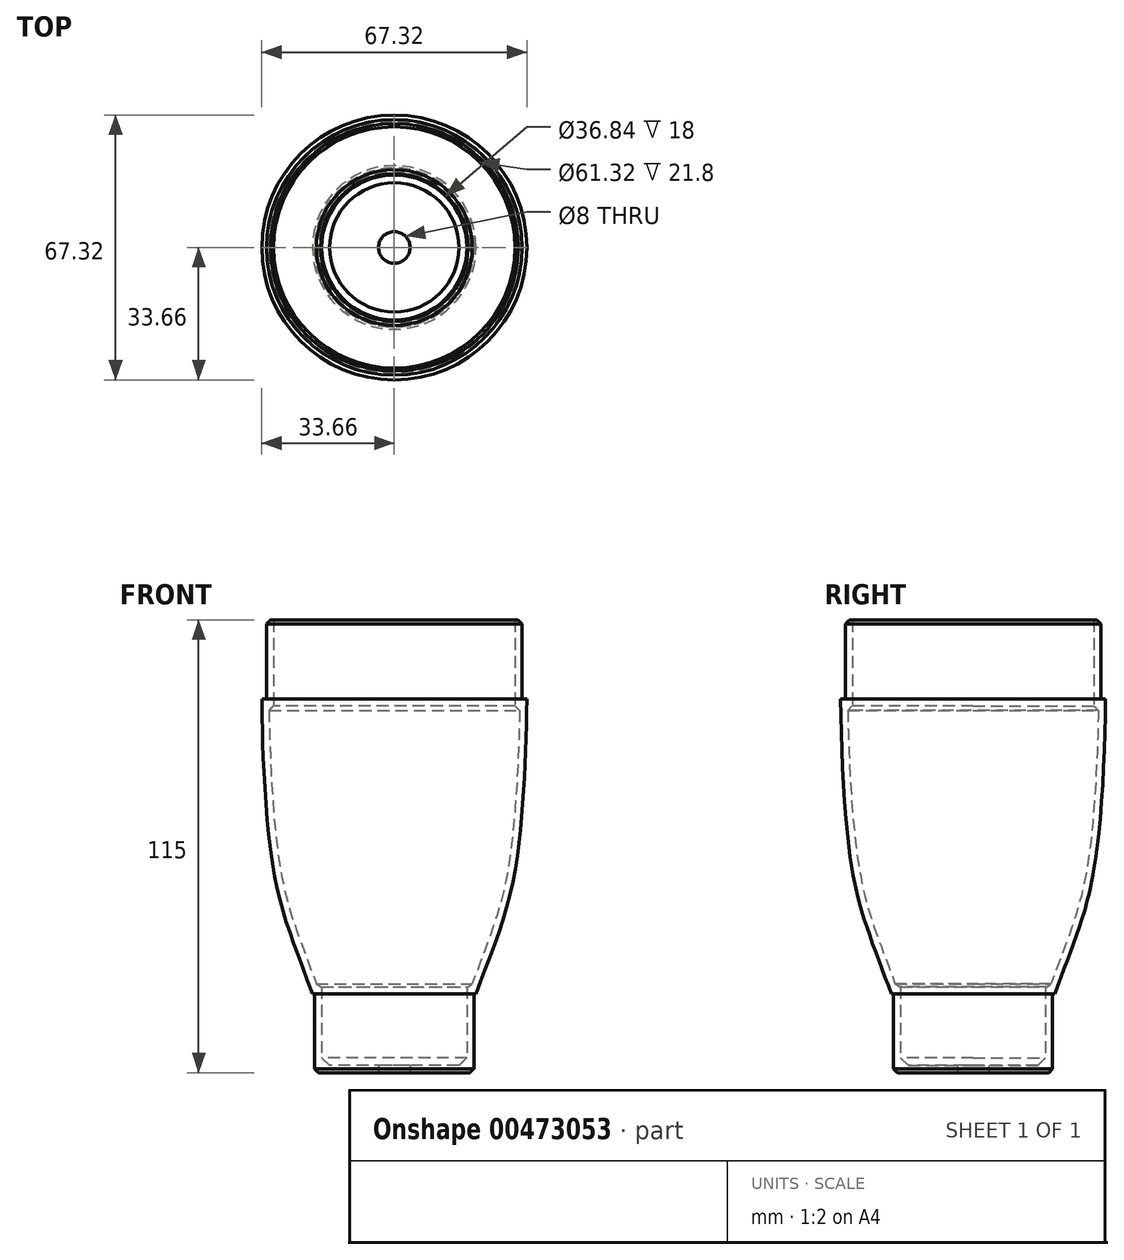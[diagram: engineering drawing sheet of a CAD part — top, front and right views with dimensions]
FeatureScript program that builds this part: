
annotation { "Feature Type Name" : "Feature", "Feature Type Description" : "" }
export const myFeature = defineFeature(function(context is Context, id is Id, definition is map)
    precondition{}
    {
        {
            var Q0;
            Q0=qCreatedBy(makeId("Front.planeOp"),FACE);
            var sketch = newSketch(context, id + "F0", { "sketchPlane" : qUnion([Q0])});
            skLineSegment(sketch, "E0", {"start": v(0, 0) * mm, "end": v(0, 75) * mm, "construction": true});
            skLineSegment(sketch, "E1", {"start": v(20.22, 0) * mm, "end": v(20.22, -20) * mm});
            skLineSegment(sketch, "E2", {"start": v(33.66, 75) * mm, "end": v(32.46, 75) * mm});
            skLineSegment(sketch, "E3", {"start": v(32.46, 75) * mm, "end": v(32.46, 95) * mm});
            skLineSegment(sketch, "E4", {"start": v(20.22, 0) * mm, "end": v(20.79, 0) * mm});
            skFitSpline(sketch, "E5", {"points": [v(33.65, 75) * mm, v(30.92, 32.86) * mm, v(20.79, 0) * mm], "startDerivative": vector(-0.17, -45.95) * mm, "endDerivative": vector(-30.96, -85.58) * mm});
            skLineSegment(sketch, "E6", {"start": v(0, 75) * mm, "end": v(33.66, 75) * mm, "construction": true});
            skLineSegment(sketch, "E7", {"start": v(20.22, -20) * mm, "end": v(0, -20) * mm});
            skLineSegment(sketch, "E8", {"start": v(0, -20) * mm, "end": v(0, 95) * mm});
            skLineSegment(sketch, "E9", {"start": v(0, 95) * mm, "end": v(32.46, 95) * mm});
            skSolve(sketch);
        }
        {
            var Q0;
            Q0=makeQuery(id+"F0.imprint","IMPRINT",FACE,{"disambiguationData":[TD([[makeQuery(id+"F0.imprint","IMPRINT",EDGE,{"derivedFrom":sQuery(id+"F0.wireOp",EDGE,"E1")}),-1.0]])]});
            var Q1;
            Q1=sQuery(id+"F0.wireOp",EDGE,"E8");
            revolve(context, id + "F1", {"surfaceOperationType" : NewSurfaceOperationType.NEW, "entities" : qUnion([Q0]), "axis" : qUnion([Q1]), "revolveType" : RevolveType.FULL});
        }
        {
            var Q0;
            Q0=makeQuery(id+"F1.opRevolve","SWEPT_EDGE",EDGE,{"disambiguationData":[OSD([sQuery(id+"F0.wireOp",EDGE,"E1"),sQuery(id+"F0.wireOp",EDGE,"E7")])]});
            chamfer(context, id + "F2", {"entities" : qUnion([Q0]), "width" : 1 * mm, "tangentPropagation" : true});
        }
        {
            var Q0;
            Q0=makeQuery(id+"F1.opRevolve","SWEPT_FACE",FACE,{"disambiguationData":[OSD([sQuery(id+"F0.wireOp",EDGE,"E9")])]});
            shell(context, id + "F3", {"entities" : qUnion([Q0]), "thickness" : 1.8 * mm});
        }
        {
            var Q0;
            Q0=makeQuery(id+"F1.opRevolve","SWEPT_FACE",FACE,{"disambiguationData":[OSD([sQuery(id+"F0.wireOp",EDGE,"E7")])]});
            var sketch = newSketch(context, id + "F4", { "sketchPlane" : qUnion([Q0])});
            skCircle(sketch, "E10", {"center": v(0, 0) * mm, "radius": 4 * mm});
            skSolve(sketch);
        }
        {
            var Q0;
            Q0=makeQuery(id+"F4.imprint","IMPRINT",FACE,{"disambiguationData":[TD([[makeQuery(id+"F4.imprint","IMPRINT",EDGE,{"derivedFrom":sQuery(id+"F4.wireOp",EDGE,"E10")}),1.0]])]});
            extrude(context, id + "F5", {"entities" : qUnion([Q0]), "operationType" : NewBodyOperationType.REMOVE, "endBound" : BoundingType.THROUGH_ALL, "oppositeDirection" : true, "depth" : 25 * mm, "offsetDistance" : 25 * mm});
        }
        {
            var Q0;
            Q0=makeQuery(id+"F1.opRevolve","SWEPT_EDGE",EDGE,{"disambiguationData":[OSD([sQuery(id+"F0.wireOp",EDGE,"E3"),sQuery(id+"F0.wireOp",EDGE,"E9")])]});
            chamfer(context, id + "F6", {"entities" : qUnion([Q0]), "width" : 1 * mm, "tangentPropagation" : true});
        }
        {
            var Q0;
            Q0=makeQuery(id+"F3.opShell","TWEAK_EDGE",EDGE,{"derivedFrom":[makeQuery(id+"F1.opRevolve","SWEPT_FACE",FACE,{"disambiguationData":[OSD([sQuery(id+"F0.wireOp",EDGE,"E1")])]}),makeQuery(id+"F1.opRevolve","SWEPT_FACE",FACE,{"disambiguationData":[OSD([sQuery(id+"F0.wireOp",EDGE,"E7")])]})]});
            chamfer(context, id + "F7", {"entities" : qUnion([Q0]), "width" : 2 * mm, "tangentPropagation" : true});
        }
        {
            var Q0;
            Q0=makeQuery(id+"F3.opShell","OFFSET_EDGE",EDGE,{"disambiguationData":[OSD([sQuery(id+"F0.wireOp",EDGE,"E4"),sQuery(id+"F0.wireOp",EDGE,"E5")])]});
            var Q1;
            Q1=makeQuery(id+"F3.opShell","OFFSET_EDGE",EDGE,{"disambiguationData":[OSD([sQuery(id+"F0.wireOp",EDGE,"E2"),sQuery(id+"F0.wireOp",EDGE,"E5")])]});
            chamfer(context, id + "F8", {"entities" : qUnion([Q0, Q1]), "width" : 1.1 * mm, "tangentPropagation" : true});
        }
    });
